# Revit family: Door-Hydraulic-PowerLift-Hidden_Cylinder-Micro
name_source: partatom
category: Doors
units: mm (PartAtom-declared; Revit-internal decimal feet)

## family parameters
Always vertical = Yes
Classification Number = 23.30.10.00
Cut with Voids When Loaded = No
Host = Wall
Room Calculation Point = No
Shared = No

## types (12) — shared parameters
Description = Hydraulic Door - Hidden Cylinder - Micro
Function = Exterior
Manufacturer = PowerLift Hydraulic Doors
Manufacturer Fax = 507-368-1358
Model = Hidden Cylinder - Micro
URL = https://powerliftdoors.com
Wall Closure = By host

## per-type parameters (varying)
| type | Height | Rough Height | Rough Width | Width |
| 11' x 4' | 4' - 0" | 4' - 0" | 11' - 0" | 11' - 0" |
| 11' x 5' | 5' - 0" | 5' - 0" | 11' - 0" | 11' - 0" |
| 11' x 6' | 6' - 0" | 6' - 0" | 11' - 0" | 11' - 0" |
| 12' x 4' | 4' - 0" | 4' - 0" | 12' - 0" | 12' - 0" |
| 12' x 5' | 5' - 0" | 5' - 0" | 12' - 0" | 12' - 0" |
| 12' x 6' | 6' - 0" | 6' - 0" | 12' - 0" | 12' - 0" |
| 13' x 4' | 4' - 0" | 4' - 0" | 13' - 0" | 13' - 0" |
| 13' x 5' | 5' - 0" | 5' - 0" | 13' - 0" | 13' - 0" |
| 14' x 4' | 4' - 0" | 4' - 0" | 14' - 0" | 14' - 0" |
| 14' x 5' | 5' - 0" | 5' - 0" | 14' - 0" | 14' - 0" |
| 15' x 4' | 4' - 0" | 4' - 0" | 15' - 0" | 15' - 0" |
| 16' x 4' | 4' - 0" | 4' - 0" | 16' - 0" | 16' - 0" |

## geometry (parser evidence)
native form markers: Sweep x10
no freeform markers — native parametric forms only
